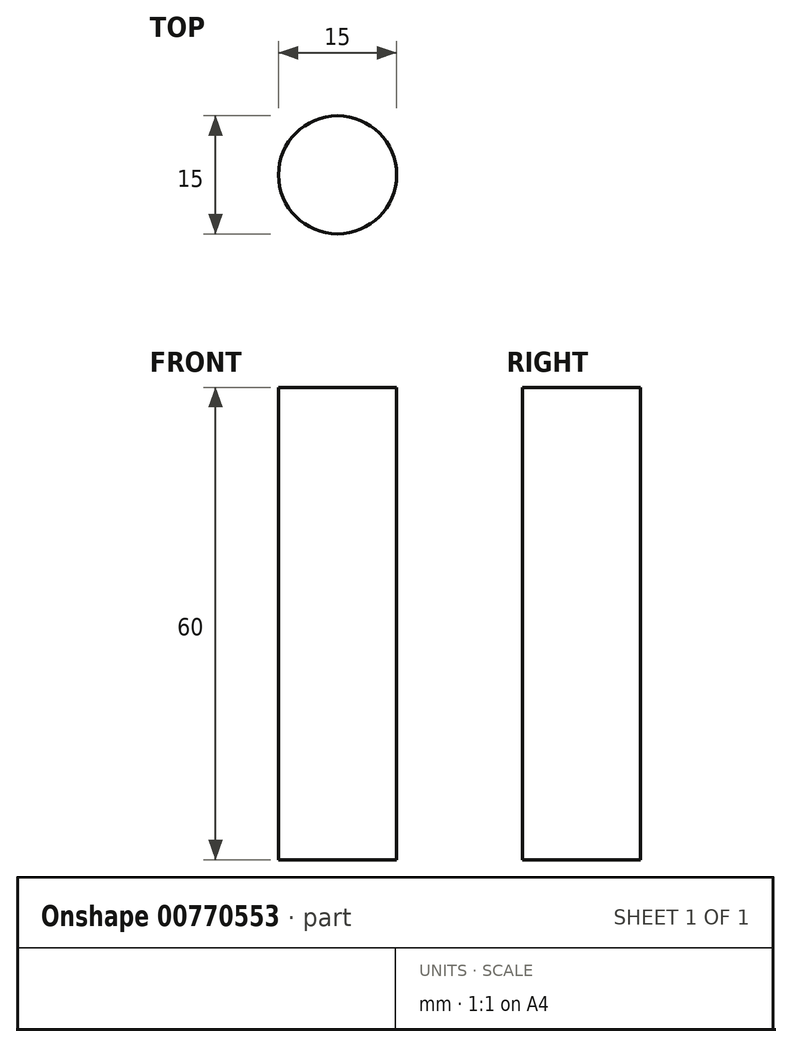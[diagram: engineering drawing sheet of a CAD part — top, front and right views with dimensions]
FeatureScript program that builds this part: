
annotation { "Feature Type Name" : "Feature", "Feature Type Description" : "" }
export const myFeature = defineFeature(function(context is Context, id is Id, definition is map)
    precondition{}
    {
        {
            var Q0;
            Q0=qCreatedBy(makeId("Top.planeOp"),FACE);
            var sketch = newSketch(context, id + "F0", { "sketchPlane" : qUnion([Q0])});
            skCircle(sketch, "E0", {"center": v(0, 0) * mm, "radius": 7.5 * mm});
            skSolve(sketch);
        }
        {
            var Q0;
            Q0 = qSketchRegion(id + "F0", true);
            extrude(context, id + "F1", {"entities" : qUnion([Q0]), "depth" : 60 * mm, "offsetDistance" : 25 * mm});
        }
    });
